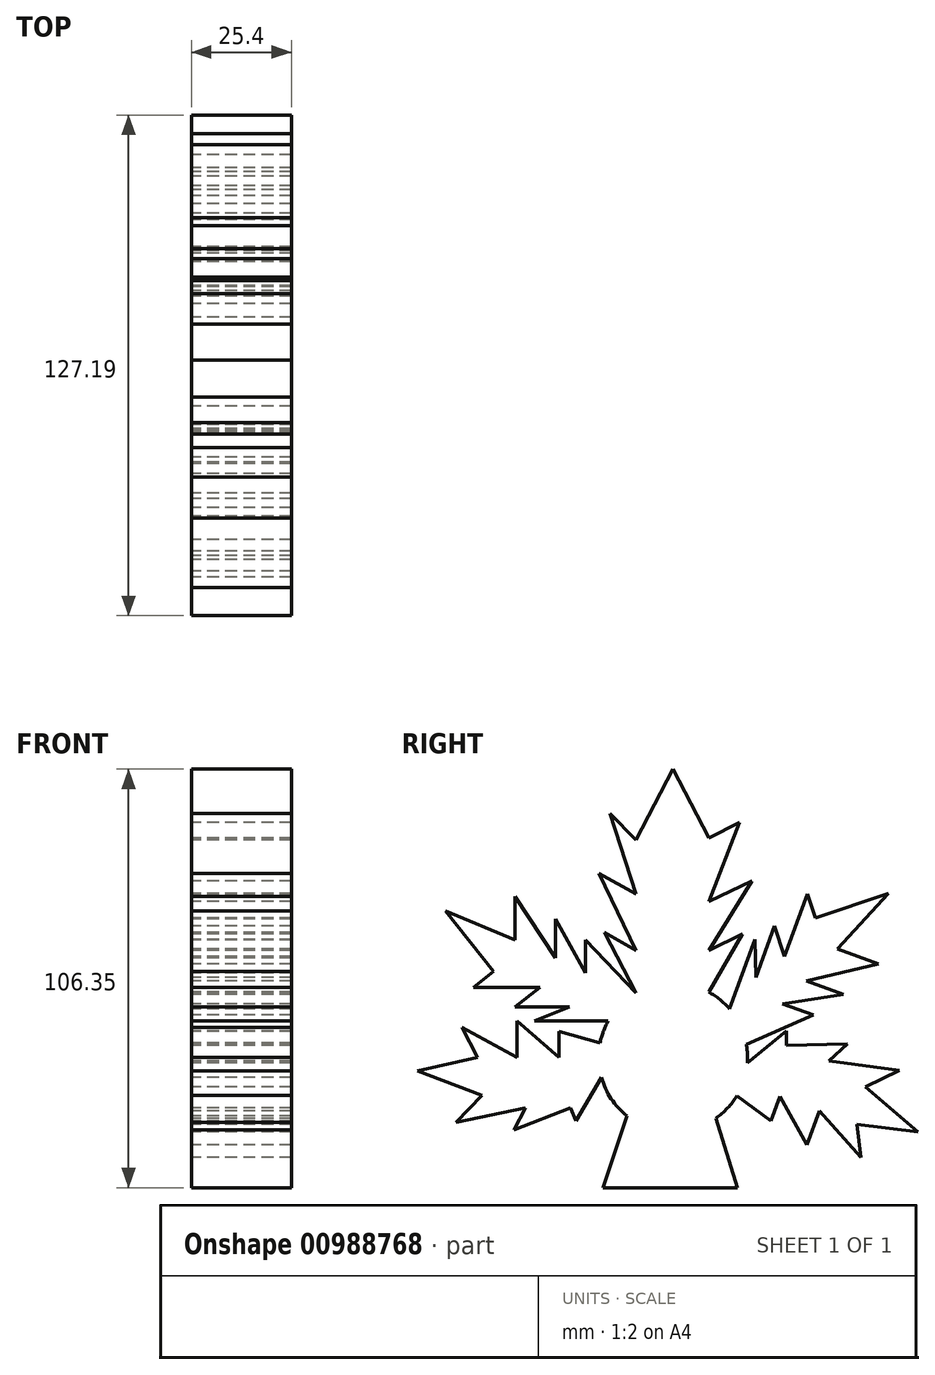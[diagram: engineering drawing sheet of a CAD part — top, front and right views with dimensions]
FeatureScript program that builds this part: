
annotation { "Feature Type Name" : "Feature", "Feature Type Description" : "" }
export const myFeature = defineFeature(function(context is Context, id is Id, definition is map)
    precondition{}
    {
        {
            var Q0;
            Q0=qCreatedBy(makeId("Right.planeOp"),FACE);
            var sketch = newSketch(context, id + "F0", { "sketchPlane" : qUnion([Q0])});
            skCircle(sketch, "E0", {"center": v(0, 0) * mm, "radius": 18.9 * mm});
            skLineSegment(sketch, "E1", {"start": v(-9.42, 16.4) * mm, "end": v(-22.3, 29.79) * mm});
            skLineSegment(sketch, "E2", {"start": v(-22.3, 29.79) * mm, "end": v(-22.3, 21.44) * mm});
            skLineSegment(sketch, "E3", {"start": v(-35.24, 9.25) * mm, "end": v(-16.5, 9.25) * mm});
            skLineSegment(sketch, "E4", {"start": v(-9.42, 16.4) * mm, "end": v(-17.41, 31.8) * mm});
            skLineSegment(sketch, "E5", {"start": v(-17.41, 31.8) * mm, "end": v(-9.42, 27.22) * mm});
            skLineSegment(sketch, "E6", {"start": v(-9.42, 27.22) * mm, "end": v(-18.85, 46.77) * mm});
            skLineSegment(sketch, "E7", {"start": v(-18.85, 46.77) * mm, "end": v(-9.42, 41.59) * mm});
            skLineSegment(sketch, "E8", {"start": v(-9.42, 41.59) * mm, "end": v(-15.97, 62.02) * mm});
            skLineSegment(sketch, "E9", {"start": v(-15.97, 62.02) * mm, "end": v(-9.42, 55.21) * mm});
            skLineSegment(sketch, "E10", {"start": v(-9.42, 55.21) * mm, "end": v(0, 73.25) * mm});
            skLineSegment(sketch, "E11", {"start": v(0, 73.25) * mm, "end": v(9.07, 55.7) * mm});
            skLineSegment(sketch, "E12", {"start": v(9.07, 55.7) * mm, "end": v(16.84, 59.7) * mm});
            skLineSegment(sketch, "E13", {"start": v(16.84, 59.7) * mm, "end": v(9.07, 39.57) * mm});
            skLineSegment(sketch, "E14", {"start": v(9.07, 39.57) * mm, "end": v(20.09, 44.89) * mm});
            skLineSegment(sketch, "E15", {"start": v(20.09, 44.89) * mm, "end": v(9.07, 27.2) * mm});
            skLineSegment(sketch, "E16", {"start": v(9.07, 27.2) * mm, "end": v(17.66, 31.34) * mm});
            skLineSegment(sketch, "E17", {"start": v(17.66, 31.34) * mm, "end": v(9.07, 16.6) * mm});
            skLineSegment(sketch, "E18", {"start": v(-22.3, 21.44) * mm, "end": v(-29.83, 35.18) * mm});
            skLineSegment(sketch, "E19", {"start": v(-29.83, 35.18) * mm, "end": v(-29.83, 25.23) * mm});
            skLineSegment(sketch, "E20", {"start": v(-29.83, 25.23) * mm, "end": v(-40.22, 40.89) * mm});
            skLineSegment(sketch, "E21", {"start": v(-40.22, 40.89) * mm, "end": v(-40.22, 29.79) * mm});
            skLineSegment(sketch, "E22", {"start": v(-40.22, 29.79) * mm, "end": v(-57.8, 37.17) * mm});
            skLineSegment(sketch, "E23", {"start": v(-57.8, 37.17) * mm, "end": v(-45.67, 21.85) * mm});
            skLineSegment(sketch, "E24", {"start": v(-45.67, 21.85) * mm, "end": v(-50.74, 17.84) * mm});
            skLineSegment(sketch, "E25", {"start": v(-50.74, 17.84) * mm, "end": v(-33.84, 17.84) * mm});
            skLineSegment(sketch, "E26", {"start": v(-33.84, 17.84) * mm, "end": v(-40.22, 12.79) * mm});
            skLineSegment(sketch, "E27", {"start": v(-40.22, 12.79) * mm, "end": v(-26.34, 12.79) * mm});
            skLineSegment(sketch, "E28", {"start": v(-26.34, 12.79) * mm, "end": v(-35.24, 9.25) * mm});
            skLineSegment(sketch, "E29", {"start": v(-18.55, 3.67) * mm, "end": v(-28.92, 6.59) * mm});
            skLineSegment(sketch, "E30", {"start": v(-28.92, 6.59) * mm, "end": v(-28.92, 0) * mm});
            skLineSegment(sketch, "E31", {"start": v(-28.92, 0) * mm, "end": v(-39.63, 9.25) * mm});
            skLineSegment(sketch, "E32", {"start": v(-39.63, 9.25) * mm, "end": v(-39.63, 0) * mm});
            skLineSegment(sketch, "E33", {"start": v(-39.63, 0) * mm, "end": v(-53.6, 7.58) * mm});
            skLineSegment(sketch, "E34", {"start": v(-53.6, 7.58) * mm, "end": v(-49.68, 0) * mm});
            skLineSegment(sketch, "E35", {"start": v(-49.68, 0) * mm, "end": v(-64.96, -3.47) * mm});
            skLineSegment(sketch, "E36", {"start": v(-64.96, -3.47) * mm, "end": v(-48.51, -9.7) * mm});
            skLineSegment(sketch, "E37", {"start": v(-48.51, -9.7) * mm, "end": v(-55.14, -16.49) * mm});
            skLineSegment(sketch, "E38", {"start": v(-55.14, -16.49) * mm, "end": v(-37.55, -12.78) * mm});
            skLineSegment(sketch, "E39", {"start": v(-37.55, -12.78) * mm, "end": v(-40.43, -18.35) * mm});
            skLineSegment(sketch, "E40", {"start": v(-40.43, -18.35) * mm, "end": v(-26.01, -12.78) * mm});
            skLineSegment(sketch, "E41", {"start": v(-26.01, -12.78) * mm, "end": v(-24.71, -16.14) * mm});
            skLineSegment(sketch, "E42", {"start": v(-24.71, -16.14) * mm, "end": v(-18.2, -5.12) * mm});
            skLineSegment(sketch, "E43.1.0", {"start": v(41.74, 27.6) * mm, "end": v(54.7, 41.6) * mm});
            skLineSegment(sketch, "E43.1.1", {"start": v(52.18, 23.8) * mm, "end": v(41.74, 27.6) * mm});
            skLineSegment(sketch, "E43.1.2", {"start": v(33.91, 19.4) * mm, "end": v(52.18, 23.8) * mm});
            skLineSegment(sketch, "E43.1.3", {"start": v(43.26, 16) * mm, "end": v(33.91, 19.4) * mm});
            skLineSegment(sketch, "E43.1.4", {"start": v(27.78, 13.63) * mm, "end": v(43.26, 16) * mm});
            skLineSegment(sketch, "E43.1.5", {"start": v(35.62, 10.77) * mm, "end": v(27.78, 13.63) * mm});
            skLineSegment(sketch, "E43.1.6", {"start": v(18.63, 3.25) * mm, "end": v(35.62, 10.77) * mm});
            skLineSegment(sketch, "E43.1.7", {"start": v(21.03, 20.38) * mm, "end": v(20.74, 29.95) * mm});
            skLineSegment(sketch, "E43.1.8", {"start": v(20.74, 29.95) * mm, "end": v(14.33, 12.34) * mm});
            skLineSegment(sketch, "E43.1.9", {"start": v(25.77, 33.42) * mm, "end": v(21.03, 20.38) * mm});
            skLineSegment(sketch, "E43.1.10", {"start": v(28.34, 25.7) * mm, "end": v(25.77, 33.42) * mm});
            skLineSegment(sketch, "E43.1.11", {"start": v(34.12, 41.58) * mm, "end": v(28.34, 25.7) * mm});
            skLineSegment(sketch, "E43.1.12", {"start": v(36.16, 35.44) * mm, "end": v(34.12, 41.58) * mm});
            skLineSegment(sketch, "E43.1.13", {"start": v(54.7, 41.6) * mm, "end": v(36.16, 35.44) * mm});
            skLineSegment(sketch, "E43.anchor1", {"start": v(0, 0) * mm, "end": v(-57.8, 37.17) * mm, "construction": true});
            skLineSegment(sketch, "E43.anchor2", {"start": v(0, 0) * mm, "end": v(54.7, 41.6) * mm, "construction": true});
            skLineSegment(sketch, "E44.1.0", {"start": v(37.24, -13.55) * mm, "end": v(47.77, -25.46) * mm});
            skLineSegment(sketch, "E44.1.1", {"start": v(47.77, -25.46) * mm, "end": v(46.68, -17) * mm});
            skLineSegment(sketch, "E44.1.2", {"start": v(46.68, -17) * mm, "end": v(62.23, -18.95) * mm});
            skLineSegment(sketch, "E44.1.3", {"start": v(62.23, -18.95) * mm, "end": v(48.9, -7.48) * mm});
            skLineSegment(sketch, "E44.1.4", {"start": v(48.9, -7.48) * mm, "end": v(57.45, -3.36) * mm});
            skLineSegment(sketch, "E44.1.5", {"start": v(57.45, -3.36) * mm, "end": v(39.66, -0.84) * mm});
            skLineSegment(sketch, "E44.1.6", {"start": v(39.66, -0.84) * mm, "end": v(44.27, 3.42) * mm});
            skLineSegment(sketch, "E44.1.7", {"start": v(44.27, 3.42) * mm, "end": v(28.82, 3.1) * mm});
            skLineSegment(sketch, "E44.1.8", {"start": v(28.82, 3.1) * mm, "end": v(28.74, 6.72) * mm});
            skLineSegment(sketch, "E44.1.9", {"start": v(16.17, -9.8) * mm, "end": v(24.93, -16.08) * mm});
            skLineSegment(sketch, "E44.1.10", {"start": v(28.74, 6.72) * mm, "end": v(18.86, -1.42) * mm});
            skLineSegment(sketch, "E44.1.11", {"start": v(27.18, -9.9) * mm, "end": v(34.08, -22.24) * mm});
            skLineSegment(sketch, "E44.1.13", {"start": v(24.93, -16.08) * mm, "end": v(27.18, -9.9) * mm});
            skLineSegment(sketch, "E44.1.14", {"start": v(34.08, -22.24) * mm, "end": v(37.24, -13.55) * mm});
            skLineSegment(sketch, "E44.anchor1", {"start": v(0, 0) * mm, "end": v(-53.6, 7.58) * mm, "construction": true});
            skLineSegment(sketch, "E44.anchor2", {"start": v(0, 0) * mm, "end": v(47.77, -25.46) * mm, "construction": true});
            skLineSegment(sketch, "E45", {"start": v(-11.71, -14.85) * mm, "end": v(-17.79, -33.1) * mm});
            skLineSegment(sketch, "E46", {"start": v(-17.79, -33.1) * mm, "end": v(16.39, -33.1) * mm});
            skLineSegment(sketch, "E47", {"start": v(16.39, -33.1) * mm, "end": v(10.91, -15.44) * mm});
            skSolve(sketch);
        }
        {
            var Q0;
            Q0 = qSketchRegion(id + "F0", true);
            extrude(context, id + "F1", {"entities" : qUnion([Q0]), "depth" : 25.4 * mm, "offsetDistance" : 25.4 * mm});
        }
    });
